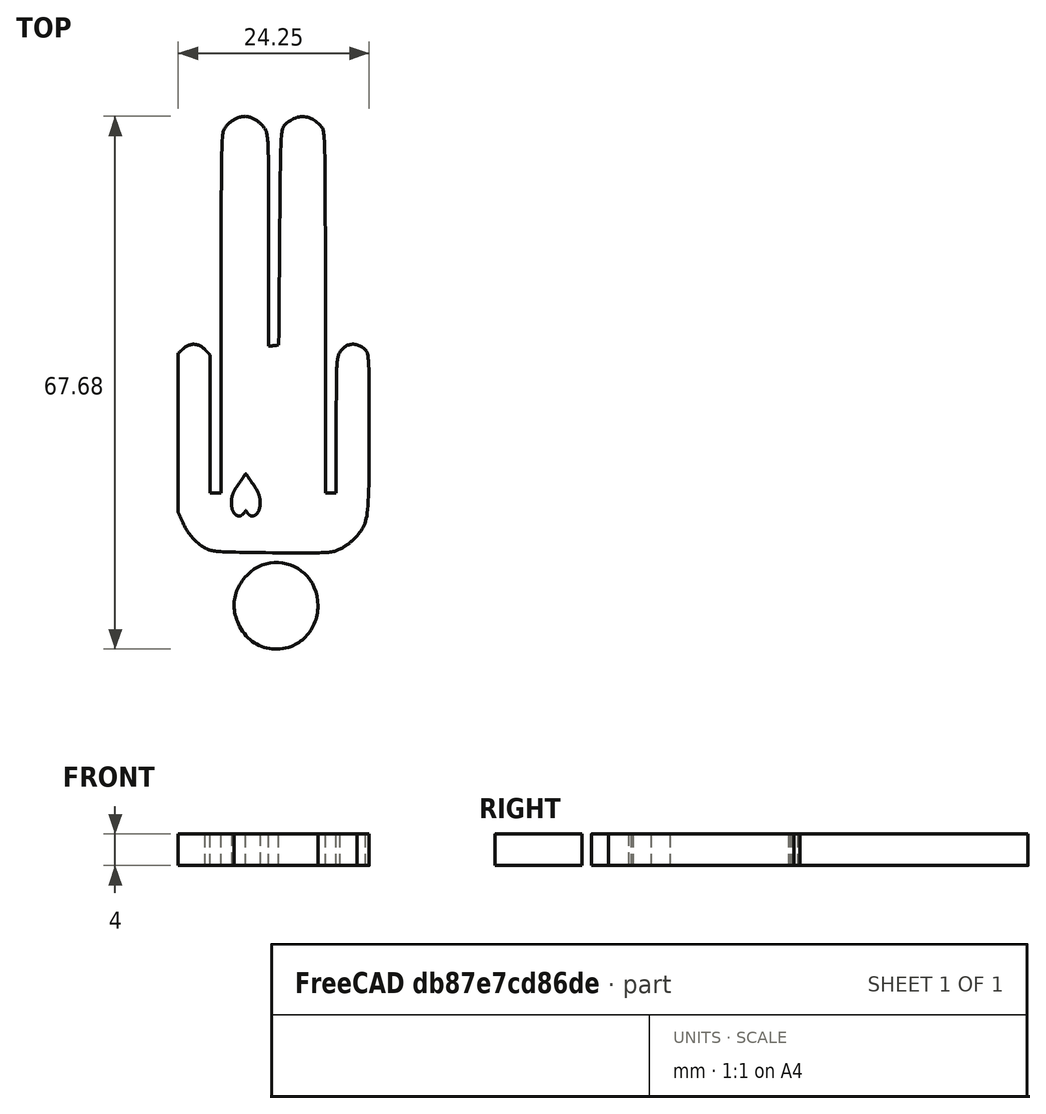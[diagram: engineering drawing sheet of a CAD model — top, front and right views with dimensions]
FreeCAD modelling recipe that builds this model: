
FCSTD DOCUMENT  (FreeCAD 0.16R6706 (Git))
Label: persona_stilizzata
License: All rights reserved
LicenseURL: http://en.wikipedia.org/wiki/All_rights_reserved
objects: Part::Extrusion×5, Part::Feature×3, Part::Fuse×3, Part::FeaturePython×3, Part::Cut×1
note: 15 computed .brp shape members not serialized (recipe doc carries the construction recipe); baked Part::Feature solids carry a one-line shape summary decoded from their .brp

FEATURE [Part::Feature] Path
  shape: bbox 16.47 x 17.59 x 2e-07 mm, 0 faces, 0 solids (baked)
FEATURE [Part::Feature] Path001
  shape: bbox 36.87 x 82.1 x 2e-07 mm, 0 faces, 0 solids (baked)
FEATURE [Part::Extrusion] Extrude
  Base = -> Path
  Dir = (0,0,10)
  Solid = true
FEATURE [Part::Extrusion] Extrude001
  Base = -> Path001
  Dir = (0,0,10)
  Solid = true
FEATURE [Part::Extrusion] Extrude002
  Base = -> Path
  Dir = (0,0,10)
  Solid = true
FEATURE [Part::Extrusion] Extrude003
  Base = -> Path001
  Dir = (0,0,10)
  Solid = true
FEATURE [Part::Fuse] Fusion
  Base = -> Extrude
  Tool = -> Extrude001
FEATURE [Part::Fuse] Fusion001
  Base = -> Extrude003
  Tool = -> Fusion
FEATURE [Part::Fuse] Fusion002
  Base = -> Extrude002
  Tool = -> Fusion001
FEATURE [Part::FeaturePython] Scale  # Draft clone (typed FeaturePython)
  Objects = -> [Fusion002]
  Scale = (5.48,3.39,1)
FEATURE [Part::Feature] Path002
  shape: bbox 153.3 x 133.6 x 2e-07 mm, 0 faces, 0 solids (baked)
FEATURE [Part::Extrusion] Extrude004
  Base = -> Path002
  Dir = (0,0,10)
  Solid = true
FEATURE [Part::FeaturePython] Scale001  # Draft clone (typed FeaturePython)
  Objects = -> [Extrude004]
  Placement = pos=(302,265,0) rot=(0,0,1;0rad)
  Scale = (0.2,0.2,1)
FEATURE [Part::Cut] Cut
  Base = -> Scale
  Tool = -> Scale001
FEATURE [Part::FeaturePython] Scale002  # Draft clone (typed FeaturePython)
  Objects = -> [Cut]
  Placement = pos=(0,0,0) rot=(0,0,1;3.14159rad)
  Scale = (0.12,0.2,0.4)
